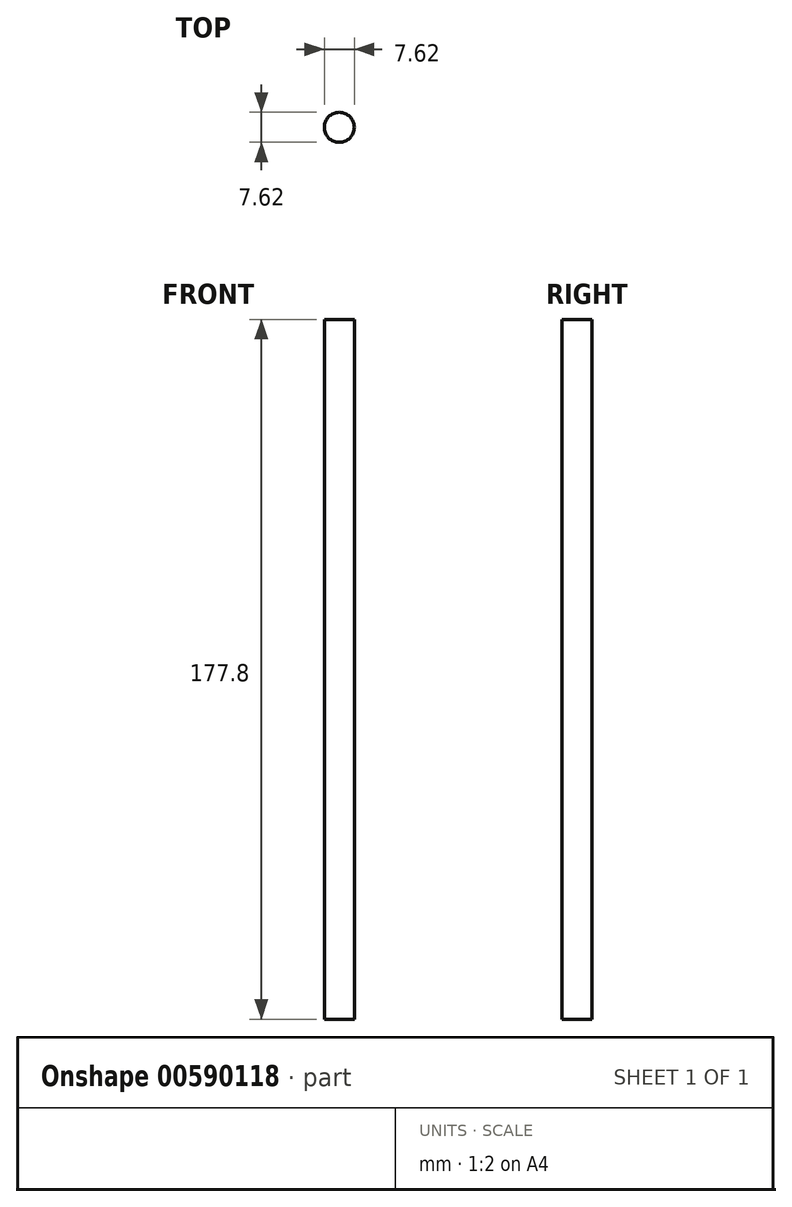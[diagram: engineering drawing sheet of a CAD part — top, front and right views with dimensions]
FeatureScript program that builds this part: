
annotation { "Feature Type Name" : "Feature", "Feature Type Description" : "" }
export const myFeature = defineFeature(function(context is Context, id is Id, definition is map)
    precondition{}
    {
        {
            var Q0;
            Q0=qCreatedBy(makeId("Front.planeOp"),FACE);
            var sketch = newSketch(context, id + "F0", { "sketchPlane" : qUnion([Q0])});
            skLineSegment(sketch, "E0", {"start": v(-43.2, 138.94) * mm, "end": v(-43.2, -38.86) * mm});
            skLineSegment(sketch, "E1", {"start": v(-43.2, -38.86) * mm, "end": v(-39.39, -38.86) * mm});
            skLineSegment(sketch, "E2", {"start": v(-39.39, -38.86) * mm, "end": v(-39.39, 138.94) * mm});
            skLineSegment(sketch, "E3", {"start": v(-39.39, 138.94) * mm, "end": v(-43.2, 138.94) * mm});
            skSolve(sketch);
        }
        {
            var Q0;
            Q0=makeQuery(id+"F0.imprint","IMPRINT",FACE,{"disambiguationData":[TD([[makeQuery(id+"F0.imprint","IMPRINT",EDGE,{"derivedFrom":sQuery(id+"F0.wireOp",EDGE,"E0")}),1.0]])]});
            var Q1;
            Q1=sQuery(id+"F0.wireOp",EDGE,"E0");
            revolve(context, id + "F1", {"entities" : qUnion([Q0]), "axis" : qUnion([Q1]), "revolveType" : RevolveType.FULL});
        }
    });
